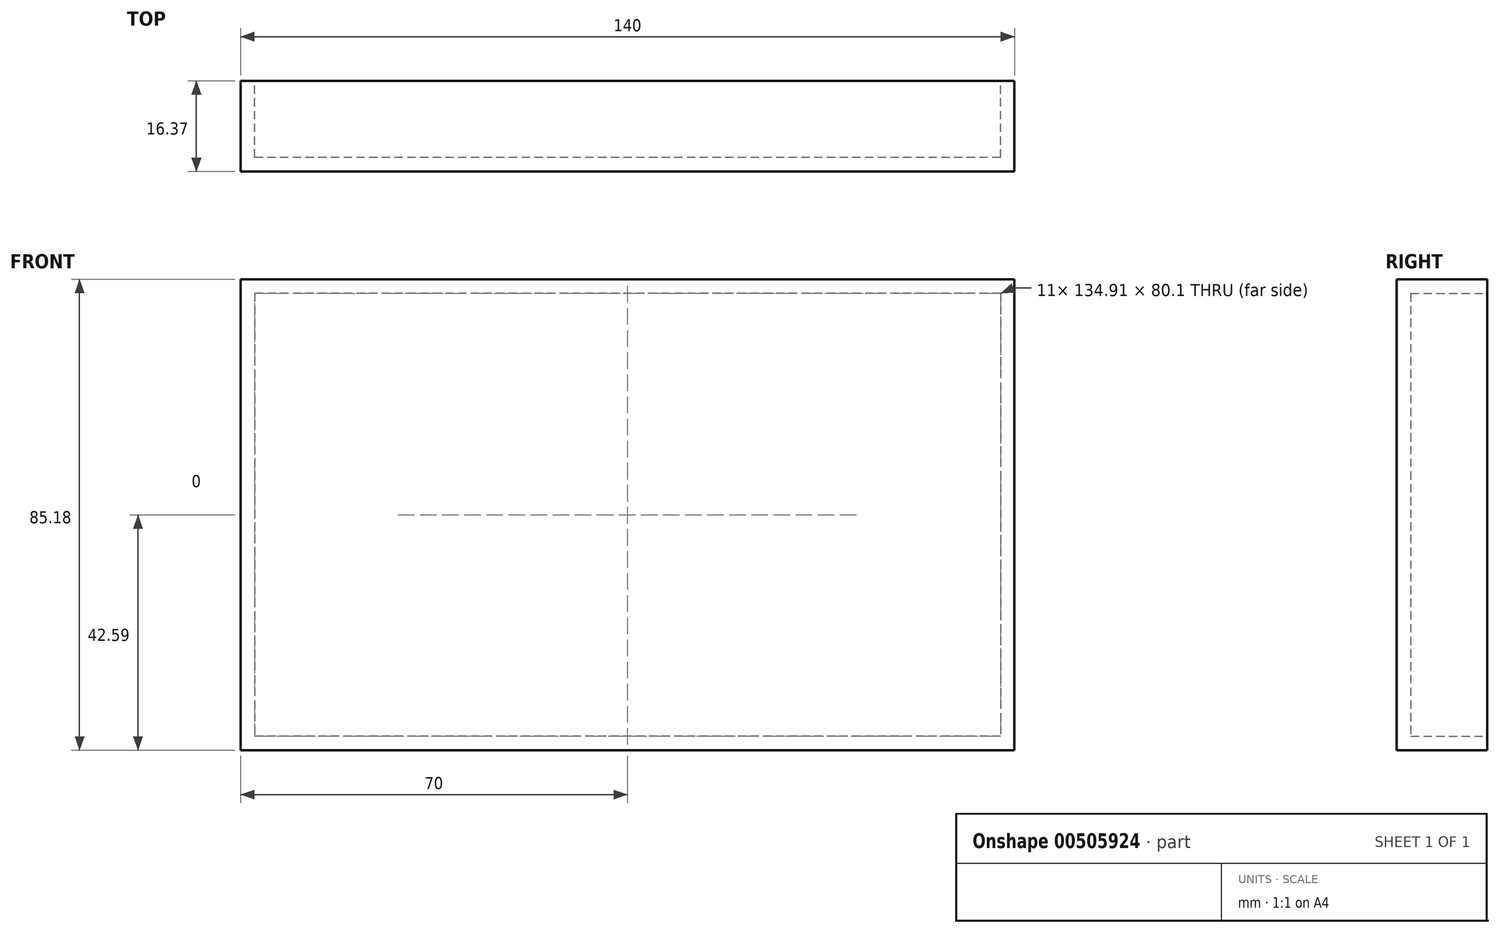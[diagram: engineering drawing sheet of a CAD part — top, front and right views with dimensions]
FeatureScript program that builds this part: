
annotation { "Feature Type Name" : "Feature", "Feature Type Description" : "" }
export const myFeature = defineFeature(function(context is Context, id is Id, definition is map)
    precondition{}
    {
        {
            var Q0;
            Q0=qCreatedBy(makeId("Front.planeOp"),FACE);
            var sketch = newSketch(context, id + "F0", { "sketchPlane" : qUnion([Q0])});
            skLineSegment(sketch, "E0.bottom", {"start": v(67.46, 40.05) * mm, "end": v(-67.46, 40.05) * mm});
            skLineSegment(sketch, "E0.top", {"start": v(67.46, -40.05) * mm, "end": v(-67.46, -40.05) * mm});
            skLineSegment(sketch, "E0.left", {"start": v(67.46, 40.05) * mm, "end": v(67.46, -40.05) * mm});
            skLineSegment(sketch, "E0.right", {"start": v(-67.46, 40.05) * mm, "end": v(-67.46, -40.05) * mm});
            skPoint(sketch, "E0.middle", {"position": v(0, 0) * mm});
            skSolve(sketch);
        }
        {
            var Q0;
            Q0 = qSketchRegion(id + "F0", true);
            extrude(context, id + "F1", {"entities" : qUnion([Q0]), "depth" : 13.83 * mm});
        }
        {
            var Q0;
            Q0=makeQuery(id+"F1.opExtrude","CAP_FACE",FACE,{"disambiguationData":[OSD([sQuery(id+"F0.wireOp",EDGE,"E0.bottom"),sQuery(id+"F0.wireOp",EDGE,"E0.top"),sQuery(id+"F0.wireOp",EDGE,"E0.left"),sQuery(id+"F0.wireOp",EDGE,"E0.right")])],"isStart":true});
            shell(context, id + "F2", {"entities" : qUnion([Q0]), "thickness" : 2.54 * mm, "oppositeDirection" : true});
        }
    });
